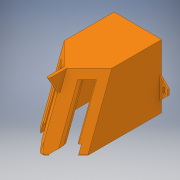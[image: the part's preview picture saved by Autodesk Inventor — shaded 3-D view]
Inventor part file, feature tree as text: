
AUTODESK INVENTOR PART (.ipt)
format: ipt  version: 2019 (Build 230136000, 136)  size: 357,376 bytes
history: native  units: in
note: dims shown in document units (in); Inventor stores cm internally (conversion verified against a paired STEP export)
features: extrude x18, sketch x15, plane x4, chamfer x3, other x2
ambient origin geometry x8: Origin, YZ Plane, XZ Plane, XY Plane, X Axis, Y Axis, Z Axis, Center Point
bodies: Solid1 (feature_tree)
feature tree (42):
  sketch  "Sketch1"  dims[d0=4.253in d1=90.0deg]
  other  "Work Axis1"
  plane  "Work Plane1"
  plane  "Work Plane2"
  extrude  "Extrusion1"  TaperAngle=90.0deg  [1 undecoded]
  extrude  "Extrusion2"  TaperAngle=180.0deg  [1 undecoded]
  sketch  "Sketch4"  dims[d6=45.0deg d7=135.0deg]
  extrude  "Extrusion3"  Depth=2.0in
  extrude  "Extrusion4"  TaperAngle=135.0deg  [1 undecoded]
  plane  "Work Plane3"
  extrude  "Extrusion5"  Depth=5.0in
  plane  "Work Plane4"
  extrude  "Extrusion6"  Depth=0.1181in TaperAngle=0.0deg
  extrude  "Extrusion7"  Depth=5.0in
  sketch  "Sketch9"  dims[d16=0.1181in d17=0.0in d18=1.0in]
  extrude  "Extrusion8"  Depth=1.0in
  extrude  "Extrusion9"  Depth=0.0787in
  extrude  "Extrusion10"  Depth=1.0in
  extrude  "Extrusion11"  Depth=0.0787in
  extrude  "Extrusion12"  Depth=2.0in
  extrude  "Extrusion13"  Depth=0.1181in TaperAngle=0.0deg
  extrude  "Extrusion14"  TaperAngle=90.0deg  [1 undecoded]
  chamfer  "Chamfer1"  Distance=7.0in
  chamfer  "Chamfer2"  Distance=7.0in
  extrude  "Extrusion15"  Depth=0.1181in
  extrude  "Extrusion16"  TaperAngle=90.0deg  [1 undecoded]
  extrude  "Extrusion17"  Depth=1.2992in
  extrude  "Extrusion18"  TaperAngle=45.0deg  [1 undecoded]
  chamfer  "Chamfer3"  Distance=1.7323in
  other  "Work Axis2"
  sketch  "Sketch2"  dims[d2=1.0in d3=180.0deg]
  sketch  "Sketch3"  dims[d4=2.0in d5=4.253in]
  sketch  "Sketch6"  dims[d8=75.0deg d9=105.0deg d10=5.0in]
  sketch  "Sketch7"  dims[d11=5.0in d12=0.1181in d13=0.0in]
  sketch  "Sketch8"  dims[d14=5.0in d15=5.0in]
  sketch  "Sketch11"  dims[d19=180.0deg d20=0.0787in]
  sketch  "Sketch12"  dims[d21=2.877in d22=1.0in]
  sketch  "Sketch13"  dims[d23=0.0in d24=0.0787in]
  sketch  "Sketch14"  dims[d25=2.877in d26=2.0in]
  sketch  "Sketch15"  dims[d27=0.0787in d28=0.1181in d29=0.0in]
  sketch  "Sketch16"  dims[d30=8.0in d31=0.0in d32=90.0deg d33=7.0in d34=0.0in]
  sketch  "Sketch17"  dims[d35=90.0deg d36=7.0in d37=0.0in d38=4.253in d39=90.0deg d40=1.2992in d41=45.0deg d42=1.7323in d43=0.0in d44=7.0in d45=0.0in d46=7.0in d47=0.0in d48=7.0in d49=0.0in d50=7.0in d51=0.0in d52=7.0in d53=0.0in d54=0.4331in d55=0.4331in d56=0.315in d57=2.5in d58=0.315in d59=2.5in d60=7.0in d61=0.0in d62=1.0in d63=90.0deg d64=1.0787in d65=90.0deg d66=0.3in d67=90.0deg d68=0.2in d69=0.0in d70=0.35in d71=0.6in d72=0.1in d73=90.0deg d74=0.1181in d75=0.0787in d76=0.0in d77=0.175in d78=0.125in d79=45.0deg d80=0.075in d81=0.125in d82=45.0deg d83=0.75in d84=90.0deg d85=150.0deg d86=0.1181in d87=0.0in d88=0.1181in d89=0.0in d90=0.1181in d91=0.0in d92=0.1181in d93=0.0in d94=0.0394in d95=0.125in d96=45.0deg]
note: 6 required parameter values undecoded (feature->parameter linkage not recoverable at this tier; creation-order binding heuristic only, values carry confidence <= 0.55)
